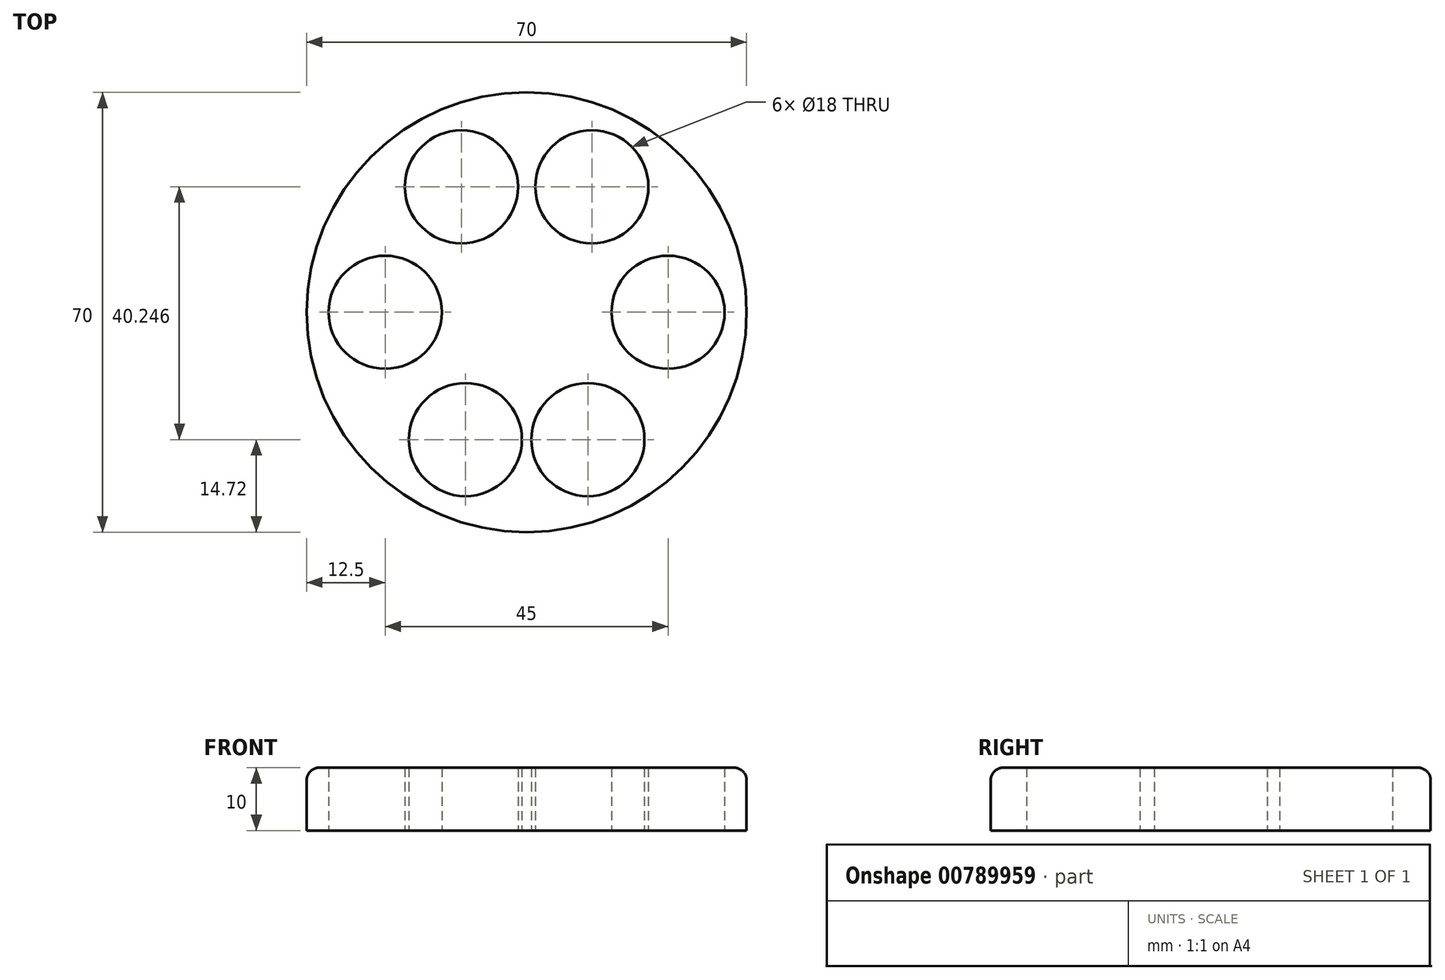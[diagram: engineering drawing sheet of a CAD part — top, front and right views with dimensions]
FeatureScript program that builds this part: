
annotation { "Feature Type Name" : "Feature", "Feature Type Description" : "" }
export const myFeature = defineFeature(function(context is Context, id is Id, definition is map)
    precondition{}
    {
        {
            var Q0;
            Q0=qCreatedBy(makeId("Top.planeOp"),FACE);
            var sketch = newSketch(context, id + "F0", { "sketchPlane" : qUnion([Q0])});
            skCircle(sketch, "E0", {"center": v(0, 0) * mm, "radius": 35 * mm});
            skCircle(sketch, "E1", {"center": v(0, 0) * mm, "radius": 22.5 * mm});
            skCircle(sketch, "E2", {"center": v(-22.5, 0) * mm, "radius": 9 * mm});
            skCircle(sketch, "E3.0.1.0", {"center": v(-10.38, 19.97) * mm, "radius": 9 * mm});
            skCircle(sketch, "E3.1.0.0", {"center": v(-9.74, -20.28) * mm, "radius": 9 * mm});
            skLineSegment(sketch, "E3.direction1", {"start": v(-22.5, 0) * mm, "end": v(-9.74, -20.28) * mm, "construction": true});
            skLineSegment(sketch, "E3.direction2", {"start": v(-22.5, 0) * mm, "end": v(-10.38, 19.97) * mm, "construction": true});
            skCircle(sketch, "E4.MirrorC", {"center": v(10.38, 19.97) * mm, "radius": 9 * mm});
            skCircle(sketch, "E5.MirrorC", {"center": v(22.5, 0) * mm, "radius": 9 * mm});
            skCircle(sketch, "E6.MirrorC", {"center": v(9.74, -20.28) * mm, "radius": 9 * mm});
            skSolve(sketch);
        }
        {
            var Q0;
            Q0=makeQuery(id+"F0.imprint","IMPRINT",FACE,{"disambiguationData":[TD([[makeQuery(id+"F0.imprint","IMPRINT",EDGE,{"derivedFrom":sQuery(id+"F0.wireOp",EDGE,"E0")}),1.0]])]});
            var Q1;
            {var subQ1=sQuery(id+"F0.wireOp",EDGE,"E1");var subQ5=sQuery(id+"F0.wireOp",EDGE,"E4.MirrorC");var subQ6=makeQuery(id+"F0.imprint","INTERSECT",VERTEX,{"disambiguationData":[OD(0.0)],"derivedFrom":[subQ1,subQ5]});Q1=makeQuery(id+"F0.imprint","IMPRINT",FACE,{"disambiguationData":[TD([[makeQuery(id+"F0.imprint","IMPRINT",EDGE,{"disambiguationData":[TD([[subQ6,1.0]])],"derivedFrom":subQ1}),1.0]])]});}
            extrude(context, id + "F1", {"entities" : qUnion([Q0, Q1]), "depth" : 10 * mm, "offsetDistance" : 25 * mm});
        }
        {
            var Q0;
            Q0=makeQuery(id+"F1.opExtrude","CAP_EDGE",EDGE,{"disambiguationData":[OSD([sQuery(id+"F0.wireOp",EDGE,"E0")])],"isStart":false});
            fillet(context, id + "F2", {"entities" : qUnion([Q0]), "radius" : 2 * mm, "tangentPropagation" : true, "allowEdgeOverflow" : false});
        }
    });
